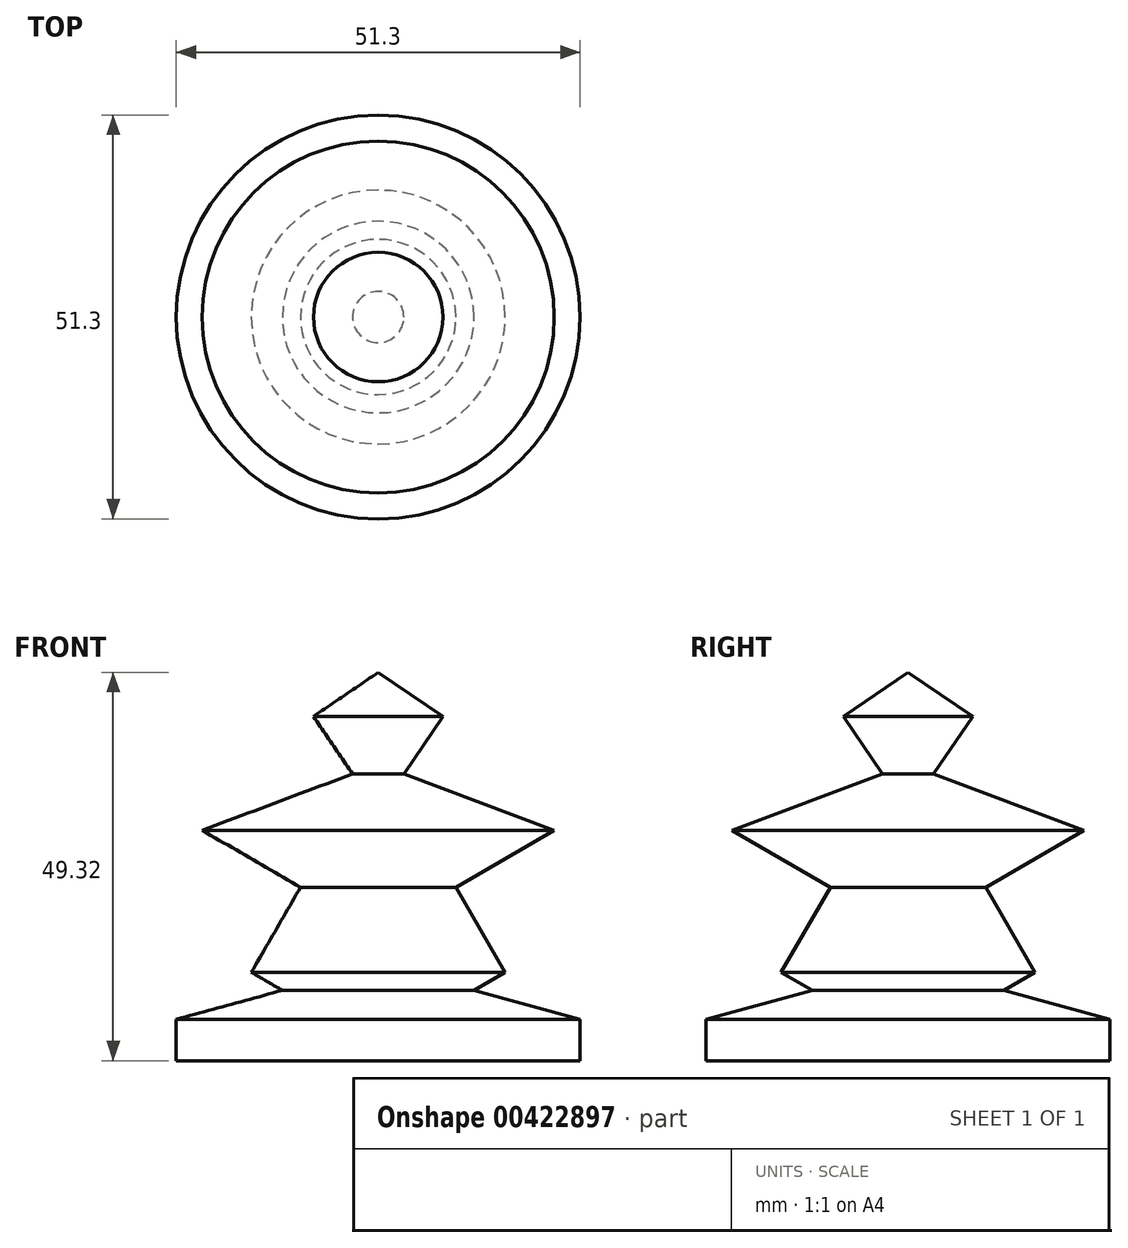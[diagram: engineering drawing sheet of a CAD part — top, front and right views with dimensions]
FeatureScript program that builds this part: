
annotation { "Feature Type Name" : "Feature", "Feature Type Description" : "" }
export const myFeature = defineFeature(function(context is Context, id is Id, definition is map)
    precondition{}
    {
        {
            var Q0;
            Q0=qCreatedBy(makeId("Front.planeOp"),FACE);
            var sketch = newSketch(context, id + "F0", { "sketchPlane" : qUnion([Q0])});
            skLineSegment(sketch, "E0", {"start": v(0, 0) * mm, "end": v(0, 49.32) * mm});
            skLineSegment(sketch, "E1", {"start": v(0, 49.32) * mm, "end": v(8.22, 43.73) * mm});
            skLineSegment(sketch, "E2", {"start": v(8.22, 43.73) * mm, "end": v(3.25, 36.43) * mm});
            skLineSegment(sketch, "E3", {"start": v(3.25, 36.43) * mm, "end": v(22.36, 29.26) * mm});
            skLineSegment(sketch, "E4", {"start": v(22.36, 29.26) * mm, "end": v(9.86, 22.03) * mm});
            skLineSegment(sketch, "E5", {"start": v(9.86, 22.03) * mm, "end": v(16.12, 11.22) * mm});
            skLineSegment(sketch, "E6", {"start": v(16.12, 11.22) * mm, "end": v(12.17, 8.93) * mm});
            skLineSegment(sketch, "E7", {"start": v(12.17, 8.93) * mm, "end": v(25.65, 5.26) * mm});
            skLineSegment(sketch, "E8", {"start": v(25.65, 5.26) * mm, "end": v(25.65, 0) * mm});
            skLineSegment(sketch, "E9", {"start": v(25.65, 0) * mm, "end": v(0, 0) * mm});
            skSolve(sketch);
        }
        {
            var Q0;
            Q0 = qSketchRegion(id + "F0", true);
            var Q1;
            Q1=sQuery(id+"F0.wireOp",EDGE,"E0");
            revolve(context, id + "F1", {"entities" : qUnion([Q0]), "axis" : qUnion([Q1]), "revolveType" : RevolveType.FULL});
        }
    });
